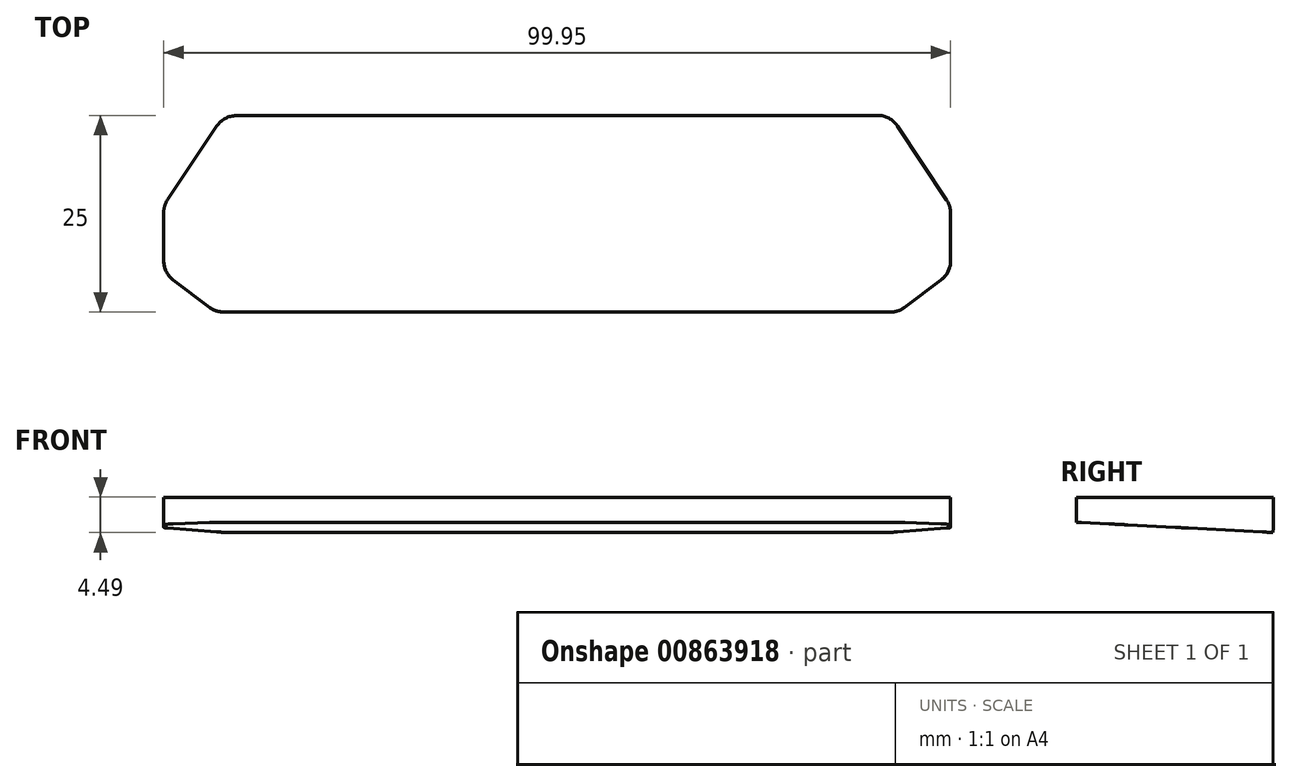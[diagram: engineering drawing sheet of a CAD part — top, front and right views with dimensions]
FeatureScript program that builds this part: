
annotation { "Feature Type Name" : "Feature", "Feature Type Description" : "" }
export const myFeature = defineFeature(function(context is Context, id is Id, definition is map)
    precondition{}
    {
        {
            var Q0;
            Q0=qCreatedBy(makeId("Top.planeOp"),FACE);
            var sketch = newSketch(context, id + "F0", { "sketchPlane" : qUnion([Q0])});
            skLineSegment(sketch, "E0.0", {"start": v(-42.35, 12.46) * mm, "end": v(0, 12.5) * mm});
            skLineSegment(sketch, "E0.1", {"start": v(42.32, 12.5) * mm, "end": v(0, 12.5) * mm});
            skLineSegment(sketch, "E0.2", {"start": v(-42.35, 12.46) * mm, "end": v(-49.97, 1.03) * mm});
            skLineSegment(sketch, "E0.3", {"start": v(42.32, 12.5) * mm, "end": v(49.98, 1) * mm});
            skLineSegment(sketch, "E0.4", {"start": v(49.98, 1) * mm, "end": v(49.98, -7.48) * mm});
            skLineSegment(sketch, "E0.5", {"start": v(49.98, -7.48) * mm, "end": v(43.33, -12.5) * mm});
            skLineSegment(sketch, "E0.6", {"start": v(-49.97, 1.03) * mm, "end": v(-49.95, -7.5) * mm});
            skLineSegment(sketch, "E0.7", {"start": v(-49.95, -7.5) * mm, "end": v(-43.35, -12.48) * mm});
            skLineSegment(sketch, "E0.8", {"start": v(-43.35, -12.48) * mm, "end": v(0, -12.5) * mm});
            skLineSegment(sketch, "E0.9", {"start": v(43.33, -12.5) * mm, "end": v(0, -12.5) * mm});
            skLineSegment(sketch, "E1", {"start": v(0, 12.5) * mm, "end": v(0, -12.5) * mm, "construction": true});
            skPoint(sketch, "E2", {"position": v(0, 0) * mm});
            skSolve(sketch);
        }
        {
            var Q0;
            Q0=makeQuery(id+"F0.imprint","IMPRINT",FACE,{"disambiguationData":[TD([[makeQuery(id+"F0.imprint","IMPRINT",EDGE,{"derivedFrom":sQuery(id+"F0.wireOp",EDGE,"E0.0")}),-1.0]])]});
            extrude(context, id + "F1", {"entities" : qUnion([Q0]), "depth" : 3.17 * mm, "offsetDistance" : 25.4 * mm});
        }
        {
            var Q0;
            Q0=qCreatedBy(makeId("Top.planeOp"),FACE);
            var sketch = newSketch(context, id + "F2", { "sketchPlane" : qUnion([Q0])});
            skLineSegment(sketch, "E3.0", {"start": v(-42.35, 12.46) * mm, "end": v(0, 12.5) * mm});
            skLineSegment(sketch, "E3.1", {"start": v(42.32, 12.5) * mm, "end": v(0, 12.5) * mm});
            skLineSegment(sketch, "E3.2", {"start": v(-42.35, 12.46) * mm, "end": v(-49.97, 1.03) * mm});
            skLineSegment(sketch, "E3.3", {"start": v(42.32, 12.5) * mm, "end": v(49.98, 1) * mm});
            skLineSegment(sketch, "E3.4", {"start": v(49.98, 1) * mm, "end": v(49.98, -7.48) * mm});
            skLineSegment(sketch, "E3.5", {"start": v(49.98, -7.48) * mm, "end": v(43.33, -12.5) * mm});
            skLineSegment(sketch, "E3.6", {"start": v(-49.97, 1.03) * mm, "end": v(-49.95, -7.5) * mm});
            skLineSegment(sketch, "E3.7", {"start": v(-49.95, -7.5) * mm, "end": v(-43.35, -12.48) * mm});
            skLineSegment(sketch, "E3.8", {"start": v(-43.35, -12.48) * mm, "end": v(0, -12.5) * mm});
            skLineSegment(sketch, "E3.9", {"start": v(43.33, -12.5) * mm, "end": v(0, -12.5) * mm});
            skLineSegment(sketch, "E4", {"start": v(0, 12.5) * mm, "end": v(0, -12.5) * mm, "construction": true});
            skPoint(sketch, "E5", {"position": v(0, 0) * mm});
            skSolve(sketch);
        }
        {
            var Q0;
            Q0 = qSketchRegion(id + "F2", true);
            var Q1;
            Q1=sQuery(id+"F2.wireOp",EDGE,"E3.9");
            revolve(context, id + "F3", {"operationType" : NewBodyOperationType.ADD, "surfaceOperationType" : NewSurfaceOperationType.NEW, "entities" : qUnion([Q0]), "axis" : qUnion([Q1]), "revolveType" : RevolveType.ONE_DIRECTION, "angle" : 3 * degree});
        }
        {
            var Q0;
            Q0=makeQuery(id+"F1.opExtrude","SWEPT_EDGE",EDGE,{"disambiguationData":[OSD([sQuery(id+"F0.wireOp",EDGE,"E0.1"),sQuery(id+"F0.wireOp",EDGE,"E0.3")])]});
            var Q1;
            Q1=makeQuery(id+"F1.opExtrude","SWEPT_EDGE",EDGE,{"disambiguationData":[OSD([sQuery(id+"F0.wireOp",EDGE,"E0.3"),sQuery(id+"F0.wireOp",EDGE,"E0.4")])]});
            var Q2;
            Q2=makeQuery(id+"F1.opExtrude","SWEPT_EDGE",EDGE,{"disambiguationData":[OSD([sQuery(id+"F0.wireOp",EDGE,"E0.4"),sQuery(id+"F0.wireOp",EDGE,"E0.5")])]});
            var Q3;
            Q3=makeQuery(id+"F1.opExtrude","SWEPT_EDGE",EDGE,{"disambiguationData":[OSD([sQuery(id+"F0.wireOp",EDGE,"E0.5"),sQuery(id+"F0.wireOp",EDGE,"E0.9")])]});
            var Q4;
            Q4=makeQuery(id+"F1.opExtrude","SWEPT_EDGE",EDGE,{"disambiguationData":[OSD([sQuery(id+"F0.wireOp",EDGE,"E0.7"),sQuery(id+"F0.wireOp",EDGE,"E0.8")])]});
            var Q5;
            Q5=makeQuery(id+"F1.opExtrude","SWEPT_EDGE",EDGE,{"disambiguationData":[OSD([sQuery(id+"F0.wireOp",EDGE,"E0.2"),sQuery(id+"F0.wireOp",EDGE,"E0.6")])]});
            var Q6;
            Q6=makeQuery(id+"F1.opExtrude","SWEPT_EDGE",EDGE,{"disambiguationData":[OSD([sQuery(id+"F0.wireOp",EDGE,"E0.6"),sQuery(id+"F0.wireOp",EDGE,"E0.7")])]});
            var Q7;
            Q7=makeQuery(id+"F1.opExtrude","SWEPT_EDGE",EDGE,{"disambiguationData":[OSD([sQuery(id+"F0.wireOp",EDGE,"E0.0"),sQuery(id+"F0.wireOp",EDGE,"E0.2")])]});
            fillet(context, id + "F4", {"entities" : qUnion([Q0, Q1, Q2, Q3, Q4, Q5, Q6, Q7]), "radius" : 3 * mm, "tangentPropagation" : true, "allowEdgeOverflow" : false});
        }
    });
